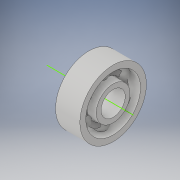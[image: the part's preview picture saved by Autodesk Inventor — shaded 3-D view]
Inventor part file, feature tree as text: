
AUTODESK INVENTOR PART (.ipt)
format: ipt  version: 2018 (Build 220112000, 112)  size: 444,416 bytes
history: native  units: in
note: dims shown in document units (in); Inventor stores cm internally (conversion verified against a paired STEP export)
features: sketch x6, revolve x5, pattern_circular x4, boolean_combine x1
ambient origin geometry x8: Origin, YZ Plane, XZ Plane, XY Plane, X Axis, Y Axis, Z Axis, Center Point
bodies: Solid1 (feature_tree), Solid2 (feature_tree)
feature tree (16):
  revolve  "Revolution1"  [1 undecoded]
  revolve  "Revolution2"  [1 undecoded]
  sketch  "Sketch3"  dims[d4=0.028in]
  pattern_circular  "Circular Pattern1"  [2 undecoded]
  revolve  "Revolution3"  [1 undecoded]
  pattern_circular  "Circular Pattern2"  Angle=90.0deg  [1 undecoded]
  revolve  "Revolution4"  Angle=360.0deg
  pattern_circular  "Circular Pattern3"  [2 undecoded]
  revolve  "Revolution5"  Angle=45.0deg
  pattern_circular  "Circular Pattern4"  [2 undecoded]
  boolean_combine  "Combine2"
  sketch  "Sketch1"  dims[d0=0.0575in d1=0.116in]
  sketch  "Sketch2"  dims[d2=0.023in d3=0.05in]
  sketch  "Sketch4"  dims[d5=90.0deg]
  sketch  "Sketch5"  dims[d6=0.058in]
  sketch  "Sketch6"  dims[d7=0.05in d8=0.025in d9=0.048in d10=90.0deg d11=2.3622in d12=360.0deg d14=0.005in d15=45.0deg d16=0.0054in d17=90.0deg d18=2.3622in d19=360.0deg d21=0.1374in d22=2.3622in d23=360.0deg d25=90.0deg d26=2.3622in d27=360.0deg]
note: 10 required parameter values undecoded (feature->parameter linkage not recoverable at this tier; creation-order binding heuristic only, values carry confidence <= 0.55)